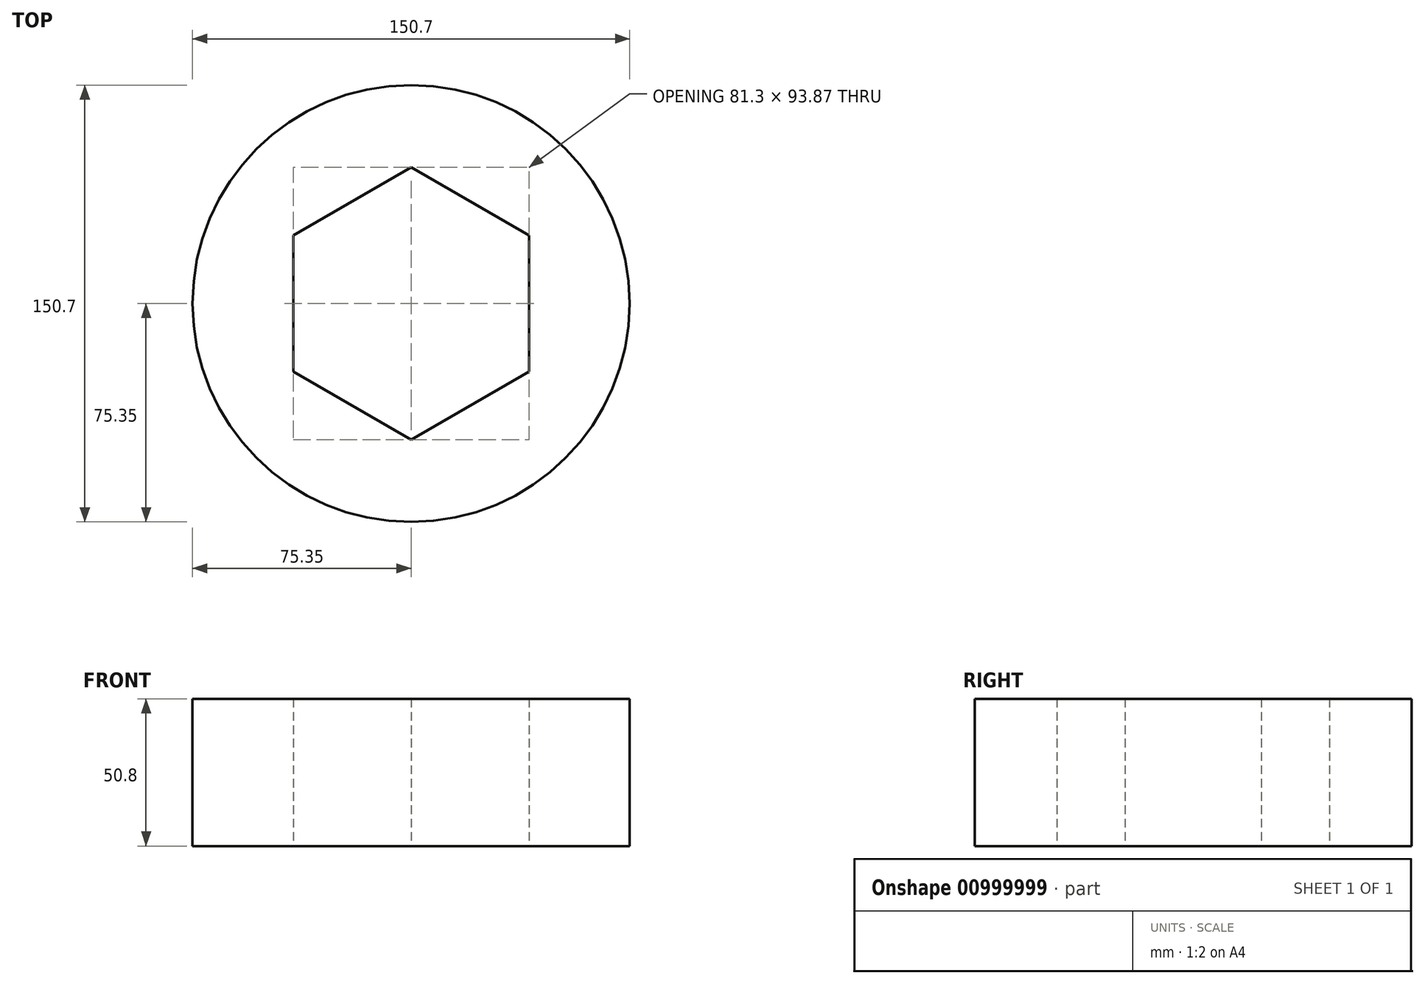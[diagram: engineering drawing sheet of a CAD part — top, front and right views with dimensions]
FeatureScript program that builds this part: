
annotation { "Feature Type Name" : "Feature", "Feature Type Description" : "" }
export const myFeature = defineFeature(function(context is Context, id is Id, definition is map)
    precondition{}
    {
        {
            var Q0;
            Q0=qCreatedBy(makeId("Top.planeOp"),FACE);
            var sketch = newSketch(context, id + "F0", { "sketchPlane" : qUnion([Q0])});
            skCircle(sketch, "E0", {"center": v(0, 0) * mm, "radius": 75.35 * mm});
            skSolve(sketch);
        }
        {
            var Q0;
            Q0=makeQuery(id+"F0.imprint","IMPRINT",FACE,{"disambiguationData":[TD([[makeQuery(id+"F0.imprint","IMPRINT",EDGE,{"derivedFrom":sQuery(id+"F0.wireOp",EDGE,"E0")}),1.0]])]});
            extrude(context, id + "F1", {"entities" : qUnion([Q0]), "depth" : 50.8 * mm, "offsetDistance" : 25.4 * mm});
        }
        {
            var Q0;
            Q0=makeQuery(id+"F1.opExtrude","CAP_FACE",FACE,{"disambiguationData":[OSD([sQuery(id+"F0.wireOp",EDGE,"E0")])],"isStart":true});
            var sketch = newSketch(context, id + "F2", { "sketchPlane" : qUnion([Q0])});
            skCircle(sketch, "E1.cCircle", {"center": v(0, 0) * mm, "radius": 40.65 * mm, "construction": true});
            skLineSegment(sketch, "E1.0", {"start": v(-40.65, -23.47) * mm, "end": v(-40.65, 23.47) * mm});
            skLineSegment(sketch, "E1.1", {"start": v(-40.65, 23.47) * mm, "end": v(0, 46.94) * mm});
            skLineSegment(sketch, "E1.2", {"start": v(0, 46.94) * mm, "end": v(40.65, 23.47) * mm});
            skLineSegment(sketch, "E1.3", {"start": v(40.65, 23.47) * mm, "end": v(40.65, -23.47) * mm});
            skLineSegment(sketch, "E1.4", {"start": v(40.65, -23.47) * mm, "end": v(0, -46.94) * mm});
            skLineSegment(sketch, "E1.5", {"start": v(0, -46.94) * mm, "end": v(-40.65, -23.47) * mm});
            skPoint(sketch, "E1.0.midPoint", {"position": v(-40.65, 0) * mm});
            skSolve(sketch);
        }
        {
            var Q0;
            Q0=makeQuery(id+"F2.imprint","IMPRINT",FACE,{"disambiguationData":[TD([[makeQuery(id+"F2.imprint","IMPRINT",EDGE,{"derivedFrom":sQuery(id+"F2.wireOp",EDGE,"E1.0")}),-1.0]])]});
            extrude(context, id + "F3", {"entities" : qUnion([Q0]), "operationType" : NewBodyOperationType.REMOVE, "oppositeDirection" : true, "depth" : 50.8 * mm, "offsetDistance" : 25.4 * mm});
        }
    });
